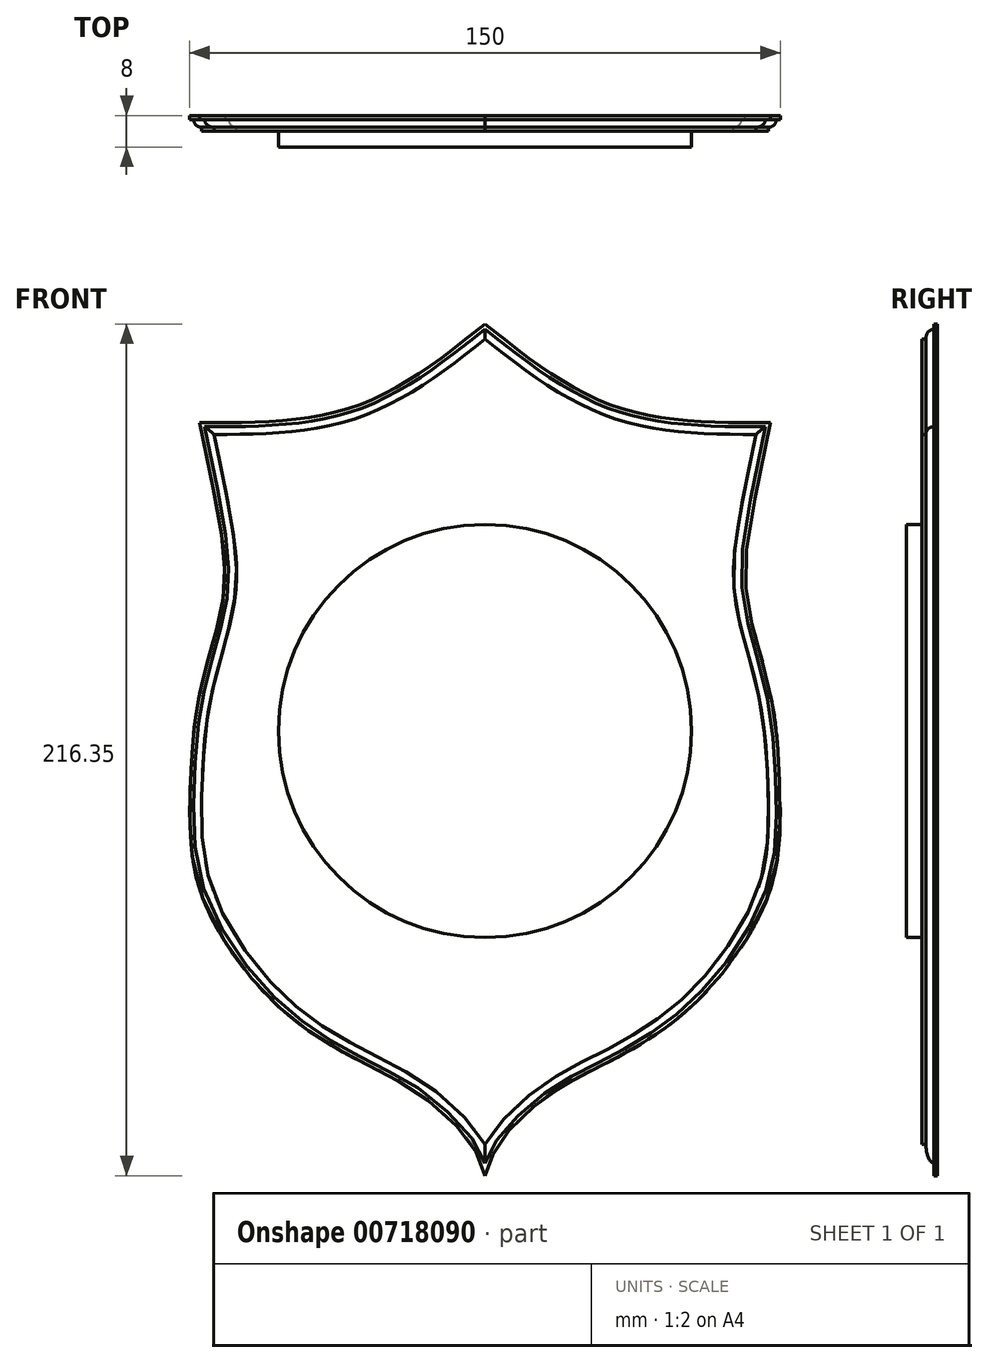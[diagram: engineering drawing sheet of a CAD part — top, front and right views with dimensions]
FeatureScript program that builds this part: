
annotation { "Feature Type Name" : "Feature", "Feature Type Description" : "" }
export const myFeature = defineFeature(function(context is Context, id is Id, definition is map)
    precondition{}
    {
        {
            var Q0;
            Q0=qCreatedBy(makeId("Front.planeOp"),FACE);
            var sketch = newSketch(context, id + "F0", { "sketchPlane" : qUnion([Q0])});
            skLineSegment(sketch, "E0", {"start": v(0, -112.97) * mm, "end": v(0, 103.38) * mm, "construction": true});
            skFitSpline(sketch, "E1", {"points": [v(0, 103.38) * mm, v(-33.18, 82.43) * mm, v(-72.47, 78.35) * mm], "startDerivative": vector(-63.47, -50.43) * mm, "endDerivative": vector(-81.45, 0.34) * mm});
            skFitSpline(sketch, "E2", {"points": [v(-72.47, 78.35) * mm, v(-66.59, 33.38) * mm, v(-72.47, 9.64) * mm, v(-74.91, -15.57) * mm, v(-72.47, -40.29) * mm, v(-58.02, -64.27) * mm, v(-43.58, -77) * mm, v(-29.88, -84.83) * mm, v(-16.66, -92.2) * mm, v(-3.7, -104.65) * mm, v(0, -112.97) * mm], "startDerivative": vector(111.62, -541.15) * mm, "endDerivative": vector(38.53, -123.34) * mm});
            skFitSpline(sketch, "E3.MirrorCS", {"points": [v(0, 103.38) * mm, v(33.18, 82.43) * mm, v(72.47, 78.35) * mm], "startDerivative": vector(63.47, -50.43) * mm, "endDerivative": vector(81.45, 0.34) * mm});
            skFitSpline(sketch, "E4.MirrorCS", {"points": [v(72.47, 78.35) * mm, v(66.59, 33.38) * mm, v(72.47, 9.64) * mm, v(74.91, -15.57) * mm, v(72.47, -40.29) * mm, v(58.02, -64.27) * mm, v(43.58, -77) * mm, v(29.88, -84.83) * mm, v(16.66, -92.2) * mm, v(3.7, -104.65) * mm, v(0, -112.97) * mm], "startDerivative": vector(-111.62, -541.15) * mm, "endDerivative": vector(-38.53, -123.34) * mm});
            skPoint(sketch, "E5", {"position": v(0, -4.8) * mm});
            skLineSegment(sketch, "E6", {"start": v(-75, 230) * mm, "end": v(-75, -223.9) * mm, "construction": true});
            skLineSegment(sketch, "E7.MirrorCS", {"start": v(75, 230) * mm, "end": v(75, -223.9) * mm, "construction": true});
            skCircle(sketch, "E8", {"center": v(0, 0) * mm, "radius": 52.5 * mm});
            skSolve(sketch);
        }
        {
            var Q0;
            Q0=qCreatedBy(makeId("Top.planeOp"),FACE);
            var sketch = newSketch(context, id + "F1", { "sketchPlane" : qUnion([Q0])});
            skLineSegment(sketch, "E9", {"start": v(-73.98, 0) * mm, "end": v(-73.98, 0) * mm});
            skLineSegment(sketch, "E10.bottom", {"start": v(-73.98, -1) * mm, "end": v(-72.98, -1) * mm});
            skLineSegment(sketch, "E10.top", {"start": v(-73.98, -4) * mm, "end": v(-70.98, -4) * mm});
            skLineSegment(sketch, "E10.left", {"start": v(-73.98, -1) * mm, "end": v(-73.98, -4) * mm});
            skLineSegment(sketch, "E10.right", {"start": v(-70.98, -3) * mm, "end": v(-70.98, -4) * mm});
            skArc(sketch, "E11", {"start": v(-72.98, -1) * mm, "mid": v(-72.4, -2.41) * mm, "end": v(-70.98, -3) * mm});
            skLineSegment(sketch, "E12", {"start": v(-73.98, -1) * mm, "end": v(-73.98, 0) * mm});
            skSolve(sketch);
        }
        {
            var Q0;
            Q0=qSketchRegion(id+"F0",true);
            extrude(context, id + "F2", {"entities" : qUnion([Q0]), "depth" : 4 * mm, "offsetDistance" : 25 * mm});
        }
        {
            var Q0;
            Q0=makeQuery(id+"F0.imprint","IMPRINT",FACE,{"disambiguationData":[TD([[makeQuery(id+"F0.imprint","IMPRINT",EDGE,{"derivedFrom":sQuery(id+"F0.wireOp",EDGE,"E8")}),1.0]])]});
            extrude(context, id + "F3", {"entities" : qUnion([Q0]), "operationType" : NewBodyOperationType.ADD, "depth" : 8 * mm, "offsetDistance" : 25 * mm});
        }
        {
            var Q0;
            Q0 = qSketchRegion(id + "F1", true);
            var Q1;
            Q1=sQuery(id+"F0.wireOp",EDGE,"E2");
            var Q2;
            Q2=sQuery(id+"F0.wireOp",EDGE,"E1");
            var Q3;
            Q3=sQuery(id+"F0.wireOp",EDGE,"E3.MirrorCS");
            var Q4;
            Q4=sQuery(id+"F0.wireOp",EDGE,"E4.MirrorCS");
            sweep(context, id + "F4", {"profiles" : qUnion([Q0]), "path" : qUnion([Q1, Q2, Q3, Q4])});
        }
        {
            var Q0;
            Q0=makeQuery(id+"F4.opSweep","SWEPT_BODY",BODY,{"disambiguationData":[OSD([sQuery(id+"F0.wireOp",EDGE,"E1"),sQuery(id+"F1.wireOp",EDGE,"E10.bottom"),sQuery(id+"F1.wireOp",EDGE,"E10.top"),sQuery(id+"F1.wireOp",EDGE,"E10.left"),sQuery(id+"F1.wireOp",EDGE,"E10.right"),sQuery(id+"F1.wireOp",EDGE,"E11")])]});
            var Q1;
            Q1=makeQuery(id+"F2.opExtrude","SWEPT_BODY",BODY,{"disambiguationData":[OSD([sQuery(id+"F0.wireOp",EDGE,"E1"),sQuery(id+"F0.wireOp",EDGE,"E2"),sQuery(id+"F0.wireOp",EDGE,"E3.MirrorCS"),sQuery(id+"F0.wireOp",EDGE,"E4.MirrorCS"),sQuery(id+"F0.wireOp",EDGE,"E8")])]});
            booleanBodies(context, id + "F5", {"operationType" : BooleanOperationType.SUBTRACTION, "tools" : qUnion([Q0]), "targets" : qUnion([Q1])});
        }
    });
